# Revit family: STH8361_24_STH8362_24
name_source: partatom
category: Luminárias
units: mm (PartAtom-declared; Revit-internal decimal feet)

## family parameters
Com base no plano de trabalho = Não
Compartilhado = Não
Corte com vazios quando carregada = Não
Cota do conector redondo = Utilizar diâmetro
Fonte luminosa = Sim
Manter orientação da anotação = Não
Ponto de cálculo do ambiente = Não
Sempre na vertical = Sim
Tipo de parte = Normal

## types (2) — shared parameters
Cromado = Cromado
Dimerização = 20-100%
Diâmetro = 0.04 m
Emissivo = Luz Âmbar
Fabricante = Stella
Filtro de cor = 16777215
Glass = Vidro
Grau de proteção (IP) = IP20
IRC (Índice de reprodução de cores) = >90 (R9 >50)
Modelo = Vela Lisa Filamento Dimerizável
Potência = 4 W
Troca de temperatura da cor de lâmpada com esmaecimento = <Nenhum>
URL = https://stella.com.br
Ângulo de Abertura = 280°
Ângulo de inclinação = 90.00°
zero-valued in all types: Elevação padrão

## per-type parameters (varying)
| type | Arquivo de rede fotométrica | Tensão Elétrica |
| STH8361/24 - 127V - LUZ ÂMBAR - 250lm - 280° | STELLA - STH8361-24 - VELA LISA FILAMENTO DIM.ies | 127V |
| STH8362/24 - 220V - LUZ ÂMBAR - 250lm - 280° | STELLA - STH8362-24 - VELA LISA FILAMENTO DIM.ies | 220V |
